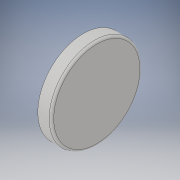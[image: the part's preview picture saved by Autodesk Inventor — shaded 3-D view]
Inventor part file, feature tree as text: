
AUTODESK INVENTOR PART (.ipt)
format: ipt  version: 2019 (Build 230136000, 136)  size: 107,520 bytes
history: native  units: mm
features: extrude x1, fillet x1, sketch x1
ambient origin geometry x8: Origin, YZ Plane, XZ Plane, XY Plane, X Axis, Y Axis, Z Axis, Center Point
bodies: Solid1 (feature_tree)
feature tree (3):
  extrude  "Extrusion1"  Depth=3.0mm TaperAngle=0.0deg
  fillet  "Fillet1"  Radius=0.5mm
  sketch  "Sketch1"  dims[d0=20.0mm d1=3.0mm d2=0.0mm d3=0.5mm]
